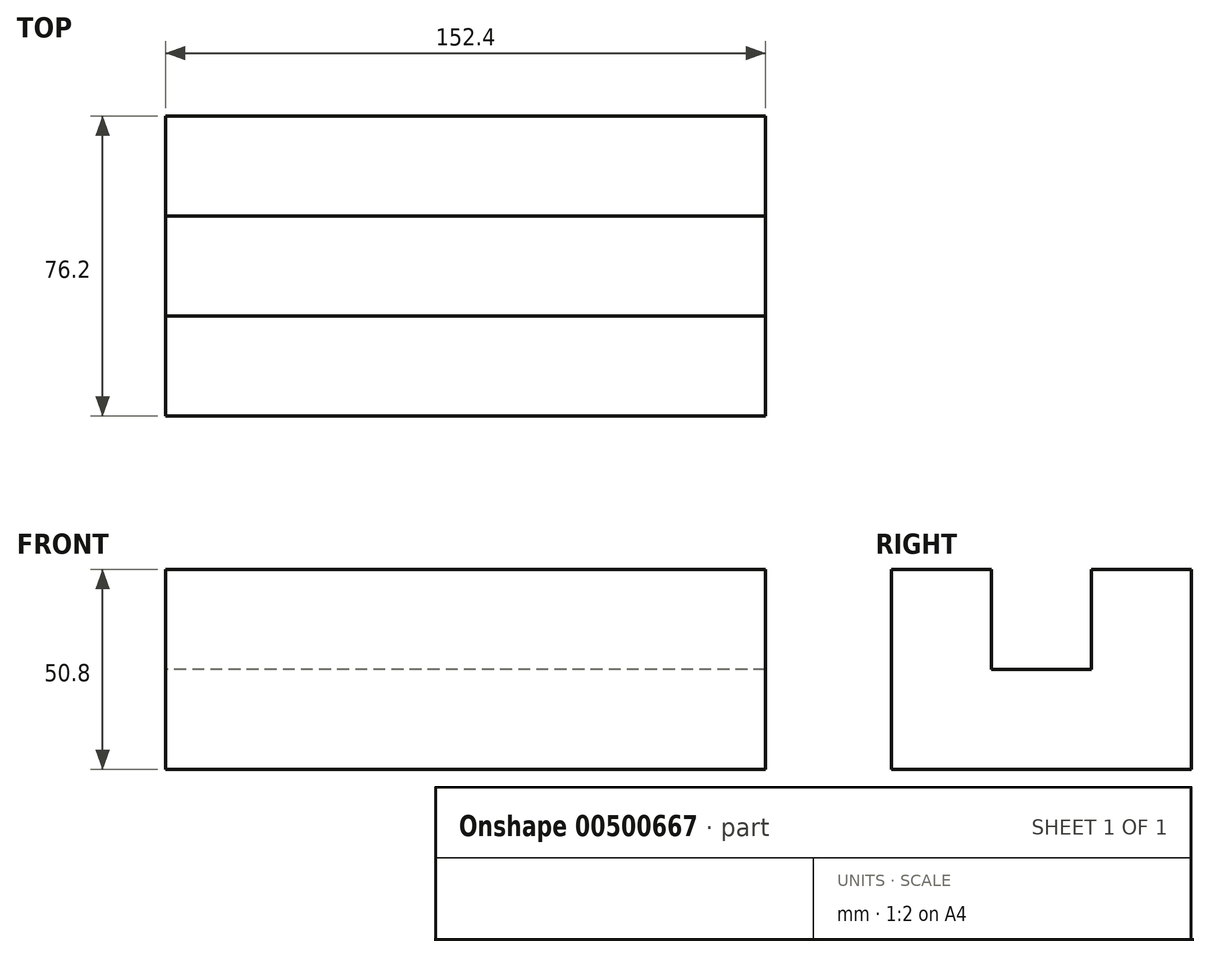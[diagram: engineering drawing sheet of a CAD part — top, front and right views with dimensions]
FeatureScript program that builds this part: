
annotation { "Feature Type Name" : "Feature", "Feature Type Description" : "" }
export const myFeature = defineFeature(function(context is Context, id is Id, definition is map)
    precondition{}
    {
        {
            var Q0;
            Q0=qCreatedBy(makeId("Right.planeOp"),FACE);
            var sketch = newSketch(context, id + "F0", { "sketchPlane" : qUnion([Q0])});
            skLineSegment(sketch, "E0", {"start": v(-52.4, 55.65) * mm, "end": v(-52.4, 4.85) * mm});
            skLineSegment(sketch, "E1", {"start": v(-52.4, 4.85) * mm, "end": v(23.8, 4.85) * mm});
            skLineSegment(sketch, "E2", {"start": v(23.8, 4.85) * mm, "end": v(23.8, 55.65) * mm});
            skLineSegment(sketch, "E3", {"start": v(23.8, 55.65) * mm, "end": v(-1.6, 55.65) * mm});
            skLineSegment(sketch, "E4", {"start": v(-1.6, 55.65) * mm, "end": v(-1.6, 30.25) * mm});
            skLineSegment(sketch, "E5", {"start": v(-1.6, 30.25) * mm, "end": v(-27, 30.25) * mm});
            skLineSegment(sketch, "E6", {"start": v(-27, 30.25) * mm, "end": v(-27, 55.65) * mm});
            skLineSegment(sketch, "E7", {"start": v(-27, 55.65) * mm, "end": v(-52.4, 55.65) * mm});
            skSolve(sketch);
        }
        {
            var Q0;
            Q0 = qSketchRegion(id + "F0", true);
            extrude(context, id + "F1", {"entities" : qUnion([Q0]), "depth" : 152.4 * mm});
        }
    });
